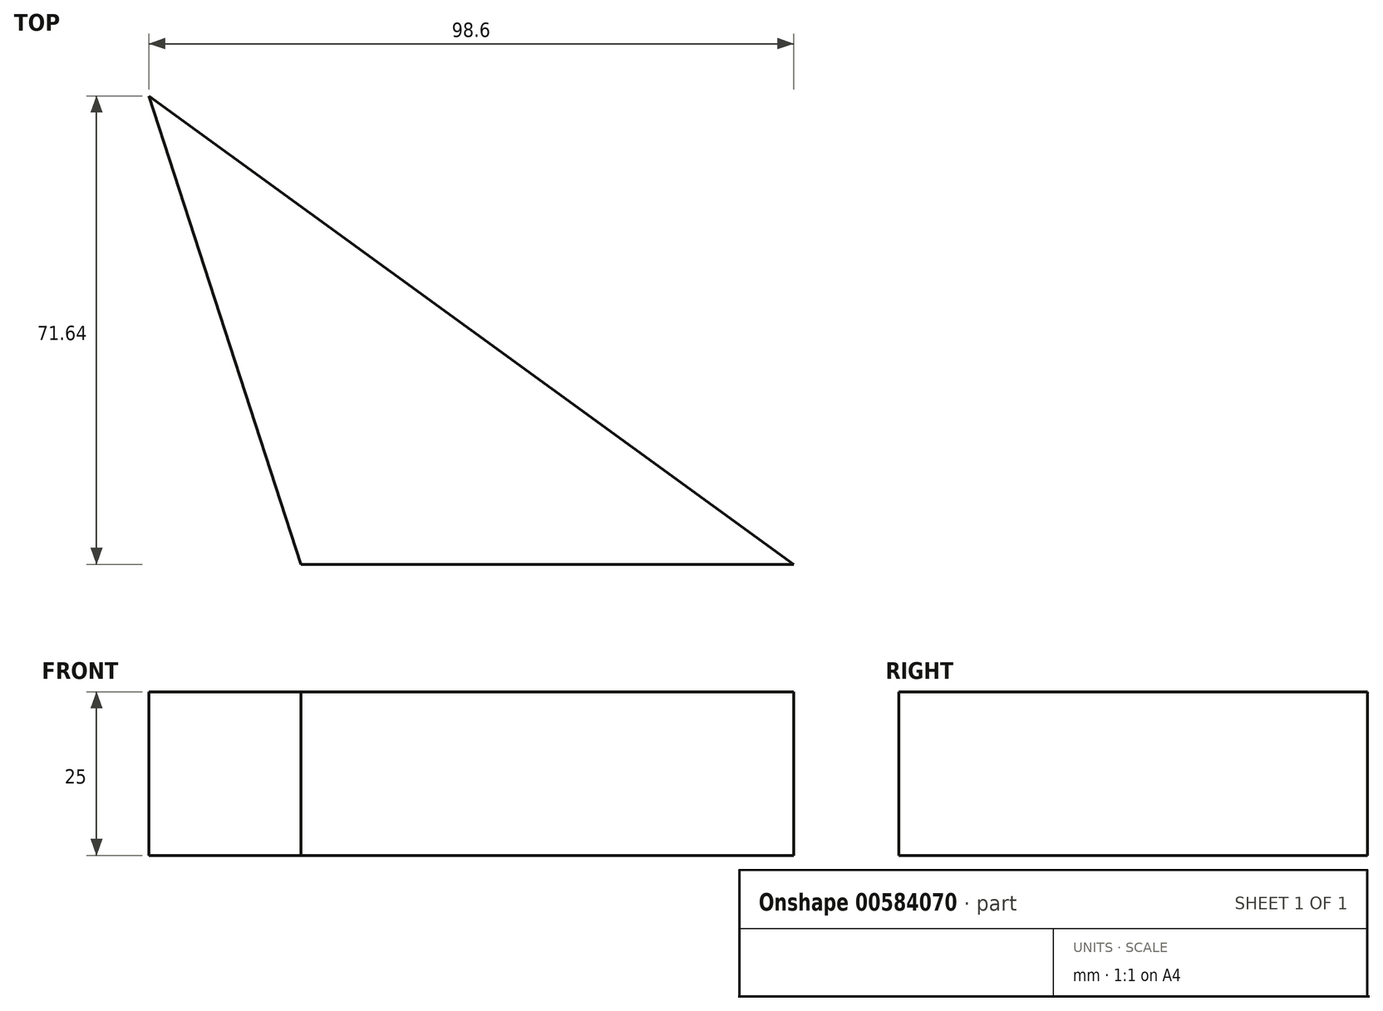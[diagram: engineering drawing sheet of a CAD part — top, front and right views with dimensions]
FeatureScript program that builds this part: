
annotation { "Feature Type Name" : "Feature", "Feature Type Description" : "" }
export const myFeature = defineFeature(function(context is Context, id is Id, definition is map)
    precondition{}
    {
        {
            var Q0;
            Q0=qCreatedBy(makeId("Top.planeOp"),FACE);
            var sketch = newSketch(context, id + "F0", { "sketchPlane" : qUnion([Q0])});
            skCircle(sketch, "E0.cCircle", {"center": v(0, 0) * mm, "radius": 19.8 * mm, "construction": true});
            skLineSegment(sketch, "E0.0", {"start": v(14.39, -19.8) * mm, "end": v(-14.39, -19.8) * mm});
            skLineSegment(sketch, "E0.1", {"start": v(-14.39, -19.8) * mm, "end": v(-23.28, 7.56) * mm});
            skLineSegment(sketch, "E0.2", {"start": v(-23.28, 7.56) * mm, "end": v(0, 24.47) * mm});
            skLineSegment(sketch, "E0.3", {"start": v(0, 24.47) * mm, "end": v(23.28, 7.56) * mm});
            skLineSegment(sketch, "E0.4", {"start": v(23.28, 7.56) * mm, "end": v(14.39, -19.8) * mm});
            skPoint(sketch, "E0.0.midPoint", {"position": v(0, -19.8) * mm});
            skLineSegment(sketch, "E1", {"start": v(-14.39, -19.8) * mm, "end": v(-43.87, 70.93) * mm});
            skLineSegment(sketch, "E2", {"start": v(23.28, 7.56) * mm, "end": v(-43.87, 56.34) * mm});
            skLineSegment(sketch, "E3", {"start": v(-43.87, 56.34) * mm, "end": v(80.82, -34.24) * mm});
            skLineSegment(sketch, "E4", {"start": v(-14.39, -19.8) * mm, "end": v(65.55, -19.8) * mm});
            skSolve(sketch);
        }
        {
            var Q0;
            {var subQ0=sQuery(id+"F0.wireOp",EDGE,"E0.2");Q0=makeQuery(id+"F0.imprint","IMPRINT",FACE,{"disambiguationData":[TD([[makeQuery(id+"F0.imprint","IMPRINT",EDGE,{"derivedFrom":subQ0}),1.0]])]});}
            var Q1;
            {var subQ1=sQuery(id+"F0.wireOp",EDGE,"E0.2");Q1=makeQuery(id+"F0.imprint","IMPRINT",FACE,{"disambiguationData":[TD([[makeQuery(id+"F0.imprint","IMPRINT",EDGE,{"derivedFrom":subQ1}),-1.0]])]});}
            var Q2;
            {var subQ0=sQuery(id+"F0.wireOp",EDGE,"E0.4");Q2=makeQuery(id+"F0.imprint","IMPRINT",FACE,{"disambiguationData":[TD([[makeQuery(id+"F0.imprint","IMPRINT",EDGE,{"derivedFrom":subQ0}),1.0]])]});}
            extrude(context, id + "F1", {"entities" : qUnion([Q0, Q1, Q2]), "depth" : 25 * mm, "offsetDistance" : 25 * mm});
        }
    });
